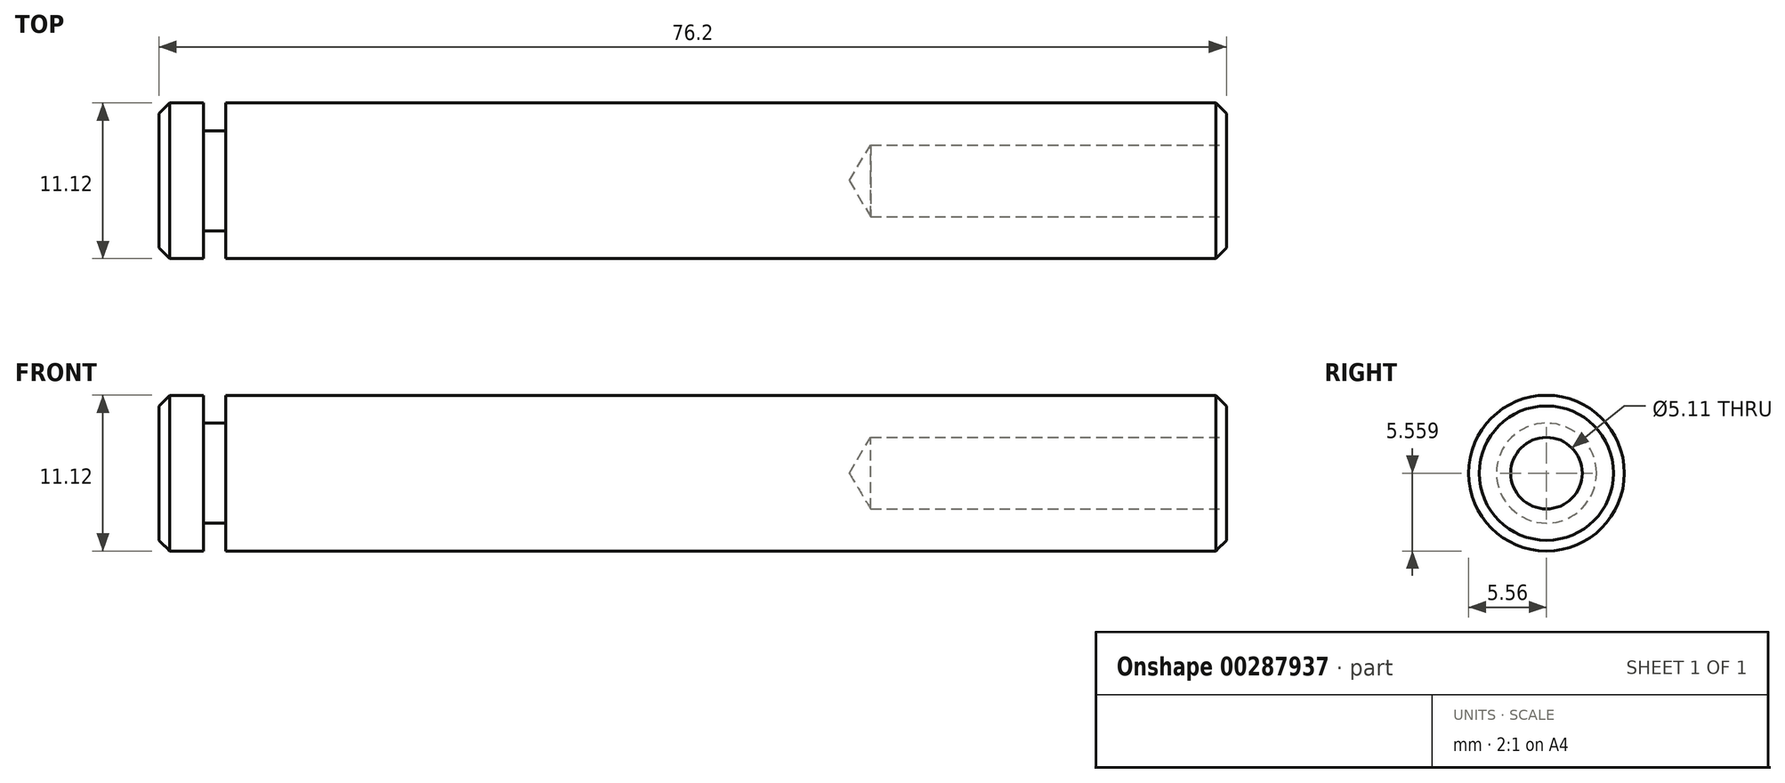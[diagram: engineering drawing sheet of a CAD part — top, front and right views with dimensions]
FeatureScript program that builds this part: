
annotation { "Feature Type Name" : "Feature", "Feature Type Description" : "" }
export const myFeature = defineFeature(function(context is Context, id is Id, definition is map)
    precondition{}
    {
        {
            var Q0;
            Q0=qCreatedBy(makeId("Front.planeOp"),FACE);
            var sketch = newSketch(context, id + "F0", { "sketchPlane" : qUnion([Q0])});
            skLineSegment(sketch, "E0.bottom", {"start": v(-62.83, 38.74) * mm, "end": v(13.37, 38.74) * mm});
            skLineSegment(sketch, "E0.top", {"start": v(-62.83, 33.18) * mm, "end": v(13.37, 33.18) * mm});
            skLineSegment(sketch, "E0.left", {"start": v(-62.83, 38.74) * mm, "end": v(-62.83, 33.18) * mm});
            skLineSegment(sketch, "E0.right", {"start": v(13.37, 38.74) * mm, "end": v(13.37, 33.18) * mm});
            skSolve(sketch);
        }
        {
            var Q0;
            Q0=makeQuery(id+"F0.imprint","IMPRINT",FACE,{"disambiguationData":[TD([[makeQuery(id+"F0.imprint","IMPRINT",EDGE,{"derivedFrom":sQuery(id+"F0.wireOp",EDGE,"E0.bottom")}),-1.0]])]});
            var Q1;
            Q1=sQuery(id+"F0.wireOp",EDGE,"E0.top");
            revolve(context, id + "F1", {"entities" : qUnion([Q0]), "axis" : qUnion([Q1]), "revolveType" : RevolveType.FULL});
        }
        {
            var Q0;
            Q0=makeQuery(id+"F1.opRevolve","SWEPT_FACE",FACE,{"disambiguationData":[OSD([sQuery(id+"F0.wireOp",EDGE,"E0.right")])]});
            var sketch = newSketch(context, id + "F2", { "sketchPlane" : qUnion([Q0])});
            skPoint(sketch, "E1", {"position": v(0, 33.18) * mm});
            skSolve(sketch);
        }
        {
            var Q0;
            Q0=makeQuery(id+"F1.opRevolve","SWEPT_FACE",FACE,{"disambiguationData":[OSD([sQuery(id+"F0.wireOp",EDGE,"E0.left")])]});
            cPlane(context, id + "F3", {"entities" : qUnion([Q0]), "cplaneType" : CPlaneType.OFFSET, "offset" : 4.76 * mm, "oppositeDirection" : true, "width" : 152.4 * mm, "height" : 152.4 * mm});
        }
        {
            var Q0;
            Q0=qCreatedBy(id+"F3.planeOp",FACE);
            var sketch = newSketch(context, id + "F4", { "sketchPlane" : qUnion([Q0])});
            skCircle(sketch, "E2", {"center": v(0, 33.18) * mm, "radius": 3.57 * mm});
            skCircle(sketch, "E3", {"center": v(0, 33.18) * mm, "radius": 8.9 * mm});
            skSolve(sketch);
        }
        {
            var Q0;
            Q0=makeQuery(id+"F4.imprint","IMPRINT",FACE,{"disambiguationData":[TD([[makeQuery(id+"F4.imprint","IMPRINT",EDGE,{"derivedFrom":sQuery(id+"F4.wireOp",EDGE,"E2")}),-1.0]])]});
            extrude(context, id + "F5", {"entities" : qUnion([Q0]), "operationType" : NewBodyOperationType.REMOVE, "depth" : 1.59 * mm, "offsetDistance" : 25.4 * mm});
        }
        {
            var Q0;
            Q0=makeQuery(id+"F1.opRevolve","SWEPT_EDGE",EDGE,{"disambiguationData":[OSD([sQuery(id+"F0.wireOp",EDGE,"E0.bottom"),sQuery(id+"F0.wireOp",EDGE,"E0.left")])]});
            var Q1;
            Q1=makeQuery(id+"F1.opRevolve","SWEPT_EDGE",EDGE,{"disambiguationData":[OSD([sQuery(id+"F0.wireOp",EDGE,"E0.bottom"),sQuery(id+"F0.wireOp",EDGE,"E0.right")])]});
            chamfer(context, id + "F6", {"entities" : qUnion([Q0, Q1]), "chamferType" : ChamferType.OFFSET_ANGLE, "width" : 0.76 * mm, "oppositeDirection" : false, "angle" : 45 * degree, "tangentPropagation" : true});
        }
        {
            var Q0;
            Q0=sQuery(id+"F2.wireOp",VERTEX,"E1");
            var Q1;
            Q1=makeQuery(id+"F1.opRevolve","SWEPT_BODY",BODY,{"disambiguationData":[OSD([sQuery(id+"F0.wireOp",EDGE,"E0.bottom"),sQuery(id+"F0.wireOp",EDGE,"E0.top"),sQuery(id+"F0.wireOp",EDGE,"E0.left"),sQuery(id+"F0.wireOp",EDGE,"E0.right")])]});
            hole(context, id + "F7", {"style" : HoleStyle.SIMPLE, "endStyle" : HoleEndStyle.BLIND, "standardTappedOrClearance" : lookupTablePath({ "standard" : "ANSI", "engagement" : "75%", "pitch" : "20 tpi", "size" : "1/4", "type" : "Tapped" }), "standardBlindInLast" : lookupTablePath({ "standard" : "ANSI", "engagement" : "75%", "pitch" : "20 tpi", "size" : "1/4", "type" : "Tapped" }), "holeDiameter" : 5.1 * mm, "majorDiameter" : 6.35 * mm, "showTappedDepth" : true, "holeDepth" : 25.4 * mm, "isTappedThrough" : true, "tappedDepth" : 21.59 * mm, "tapClearance" : 3, "locations" : qUnion([Q0]), "scope" : qUnion([Q1])});
        }
    });
